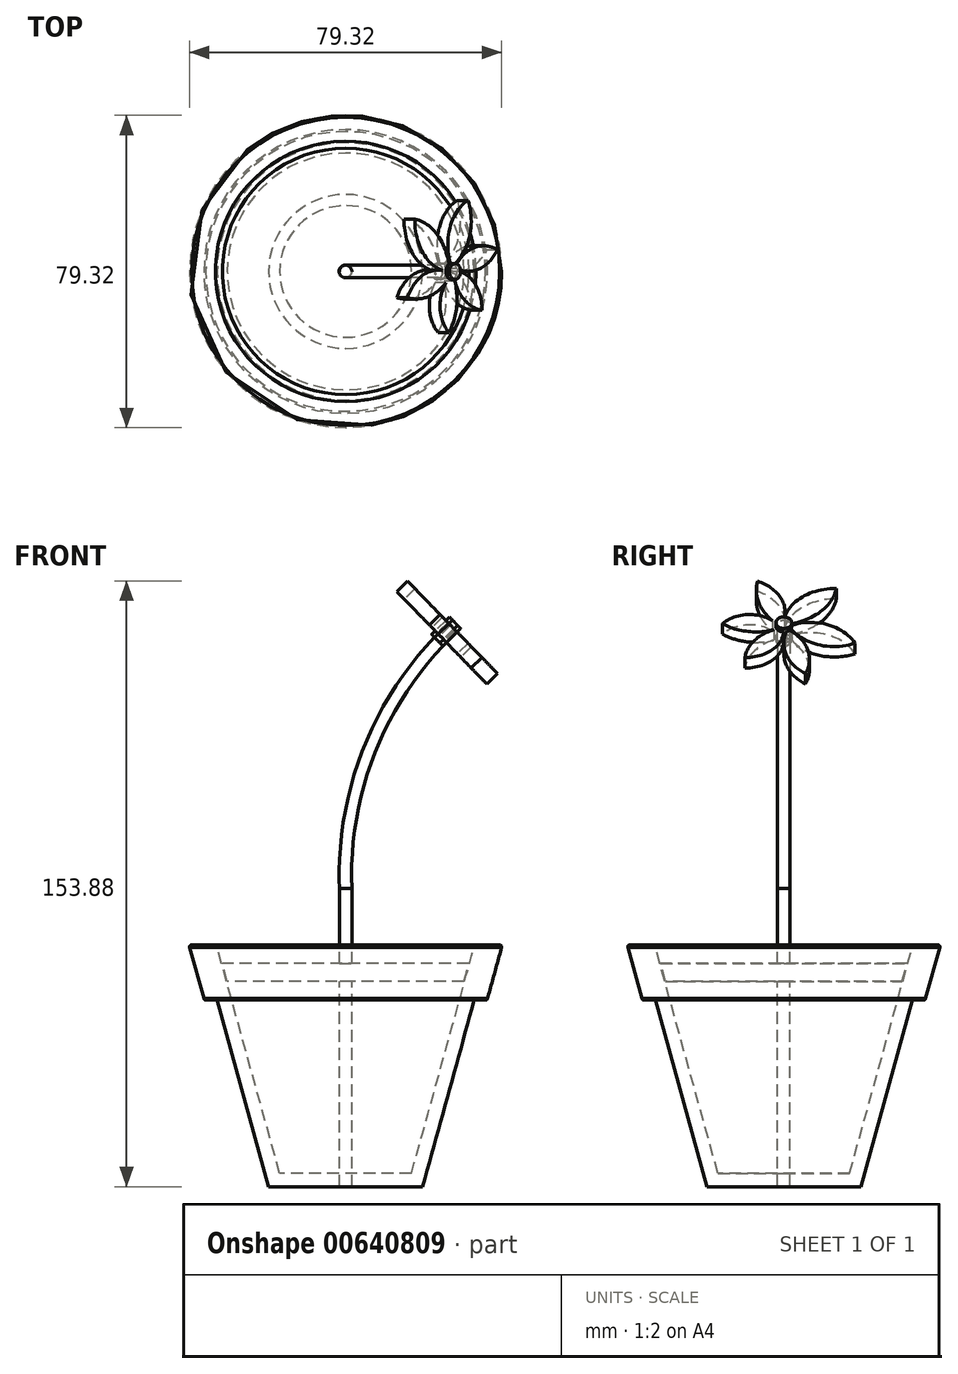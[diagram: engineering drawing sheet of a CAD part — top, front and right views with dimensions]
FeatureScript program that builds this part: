
annotation { "Feature Type Name" : "Feature", "Feature Type Description" : "" }
export const myFeature = defineFeature(function(context is Context, id is Id, definition is map)
    precondition{}
    {
        {
            var Q0;
            Q0=qCreatedBy(makeId("Front.planeOp"),FACE);
            var sketch = newSketch(context, id + "F0", { "sketchPlane" : qUnion([Q0])});
            skLineSegment(sketch, "E0", {"start": v(0, 0) * mm, "end": v(-19.55, 0) * mm});
            skLineSegment(sketch, "E1", {"start": v(0, 0) * mm, "end": v(0, 63.38) * mm});
            skLineSegment(sketch, "E2", {"start": v(-32.67, 47.4) * mm, "end": v(-19.55, 0) * mm});
            skLineSegment(sketch, "E3", {"start": v(-39.64, 60.78) * mm, "end": v(-36.03, 47.77) * mm});
            skLineSegment(sketch, "E4", {"start": v(-35.54, 47.4) * mm, "end": v(-32.67, 47.4) * mm});
            skLineSegment(sketch, "E5", {"start": v(-39.15, 61.42) * mm, "end": v(-33.1, 61.42) * mm});
            skLineSegment(sketch, "E6", {"start": v(-32.73, 61.15) * mm, "end": v(-16.73, 3.38) * mm});
            skLineSegment(sketch, "E7", {"start": v(-16.73, 3.38) * mm, "end": v(0, 3.38) * mm});
            skLineSegment(sketch, "E8", {"start": v(0, 3.38) * mm, "end": v(0, 0) * mm});
            skPoint(sketch, "E9.visualSharp", {"position": v(-39.81, 61.42) * mm});
            skArc(sketch, "E9.filletArc", {"start": v(-39.15, 61.42) * mm, "mid": v(-39.55, 61.22) * mm, "end": v(-39.64, 60.78) * mm});
            skPoint(sketch, "E10.visualSharp", {"position": v(-35.93, 47.4) * mm});
            skArc(sketch, "E10.filletArc", {"start": v(-36.03, 47.77) * mm, "mid": v(-35.85, 47.5) * mm, "end": v(-35.54, 47.4) * mm});
            skPoint(sketch, "E11.visualSharp", {"position": v(-32.81, 61.42) * mm});
            skArc(sketch, "E11.filletArc", {"start": v(-32.73, 61.15) * mm, "mid": v(-32.87, 61.35) * mm, "end": v(-33.1, 61.42) * mm});
            skSolve(sketch);
        }
        {
            var Q0;
            Q0=makeQuery(id+"F0.imprint","IMPRINT",FACE,{"disambiguationData":[TD([[makeQuery(id+"F0.imprint","IMPRINT",EDGE,{"derivedFrom":sQuery(id+"F0.wireOp",EDGE,"E0")}),-1.0]])]});
            var Q1;
            Q1=sQuery(id+"F0.wireOp",EDGE,"E8");
            revolve(context, id + "F1", {"entities" : qUnion([Q0]), "axis" : qUnion([Q1]), "revolveType" : RevolveType.FULL});
        }
        {
            var Q0;
            Q0=qCreatedBy(makeId("Front.planeOp"),FACE);
            var sketch = newSketch(context, id + "F2", { "sketchPlane" : qUnion([Q0])});
            skLineSegment(sketch, "E12", {"start": v(0, 3.35) * mm, "end": v(0, 79.16) * mm});
            skArc(sketch, "E13", {"start": v(26.04, 140.8) * mm, "mid": v(6.78, 112.61) * mm, "end": v(0, 79.16) * mm});
            skSolve(sketch);
        }
        {
            var Q0;
            Q0=qCreatedBy(makeId("Top.planeOp"),FACE);
            var sketch = newSketch(context, id + "F3", { "sketchPlane" : qUnion([Q0])});
            skCircle(sketch, "E14", {"center": v(0, 0) * mm, "radius": 1.58 * mm});
            skSolve(sketch);
        }
        {
            var Q0;
            Q0=makeQuery(id+"F3.imprint","IMPRINT",FACE,{"disambiguationData":[TD([[makeQuery(id+"F3.imprint","IMPRINT",EDGE,{"derivedFrom":sQuery(id+"F3.wireOp",EDGE,"E14")}),1.0]])]});
            var Q1;
            Q1=sQuery(id+"F2.wireOp",EDGE,"E12");
            var Q2;
            Q2=sQuery(id+"F2.wireOp",EDGE,"E13");
            sweep(context, id + "F4", {"profiles" : qUnion([Q0]), "path" : qUnion([Q1, Q2])});
        }
        {
            var Q0;
            Q0=makeQuery(id+"F4.opSweep","CAP_FACE",FACE,{"disambiguationData":[OSD([sQuery(id+"F2.wireOp",VERTEX,"E13.start"),sQuery(id+"F3.wireOp",EDGE,"E14")])],"isStart":false});
            cPlane(context, id + "F5", {"entities" : qUnion([Q0]), "cplaneType" : CPlaneType.OFFSET, "offset" : 1.27 * mm, "width" : 152.4 * mm, "height" : 152.4 * mm});
        }
        {
            var Q0;
            Q0=qCreatedBy(id+"F5.planeOp",FACE);
            var sketch = newSketch(context, id + "F6", { "sketchPlane" : qUnion([Q0])});
            skCircle(sketch, "E15", {"center": v(0, 83.3) * mm, "radius": 2.03 * mm});
            skArc(sketch, "E16", {"start": v(13.33, 96.65) * mm, "mid": v(4.5, 93.53) * mm, "end": v(0, 85.33) * mm});
            skArc(sketch, "E17", {"start": v(1.81, 84.2) * mm, "mid": v(9.5, 88.64) * mm, "end": v(13.33, 96.65) * mm});
            skArc(sketch, "E18", {"start": v(18.04, 77.24) * mm, "mid": v(11.26, 83.82) * mm, "end": v(1.81, 83.56) * mm});
            skArc(sketch, "E19", {"start": v(1.81, 82.4) * mm, "mid": v(8.93, 76.69) * mm, "end": v(18.04, 77.24) * mm});
            skArc(sketch, "E20", {"start": v(5.47, 66.5) * mm, "mid": v(6.1, 74.88) * mm, "end": v(1.43, 81.86) * mm});
            skArc(sketch, "E21", {"start": v(0.65, 81.38) * mm, "mid": v(0.66, 73.16) * mm, "end": v(5.47, 66.5) * mm});
            skArc(sketch, "E22", {"start": v(-9.88, 72.2) * mm, "mid": v(-3.14, 74.77) * mm, "end": v(0, 81.27) * mm});
            skArc(sketch, "E23", {"start": v(-1.8, 82.37) * mm, "mid": v(-7.3, 78.45) * mm, "end": v(-9.88, 72.2) * mm});
            skArc(sketch, "E24", {"start": v(-15.56, 84.23) * mm, "mid": v(-8.94, 81.42) * mm, "end": v(-1.8, 82.37) * mm});
            skArc(sketch, "E25", {"start": v(-1.8, 84.23) * mm, "mid": v(-8.68, 87.47) * mm, "end": v(-15.56, 84.23) * mm});
            skArc(sketch, "E26", {"start": v(-6.68, 99.33) * mm, "mid": v(-6.21, 91.14) * mm, "end": v(-1.8, 84.23) * mm});
            skArc(sketch, "E27", {"start": v(0, 85.33) * mm, "mid": v(-0.86, 93.51) * mm, "end": v(-6.68, 99.33) * mm});
            skSolve(sketch);
        }
        {
            var Q0;
            {var subQ0=sQuery(id+"F6.wireOp",EDGE,"E15");var subQ11=makeQuery(id+"F6.imprint","INTERSECT",VERTEX,{"derivedFrom":[subQ0,sQuery(id+"F6.wireOp",EDGE,"E17")]});Q0=makeQuery(id+"F6.imprint","IMPRINT",FACE,{"disambiguationData":[TD([[makeQuery(id+"F6.imprint","IMPRINT",EDGE,{"disambiguationData":[TD([[subQ11,1.0]])],"derivedFrom":subQ0}),1.0]])]});}
            extrude(context, id + "F7", {"entities" : qUnion([Q0]), "endBound" : BoundingType.SYMMETRIC, "depth" : 2.54 * mm, "offsetDistance" : 25.4 * mm});
        }
        {
            var Q0;
            Q0 = qSketchRegion(id + "F6", true);
            var Q1;
            Q1=makeQuery(id+"F7.opExtrude","CAP_FACE",FACE,{"disambiguationData":[OSD([sQuery(id+"F6.wireOp",EDGE,"E15"),sQuery(id+"F6.wireOp",EDGE,"E25"),sQuery(id+"F6.wireOp",EDGE,"E26")])],"isStart":false});
            extrude(context, id + "F8", {"entities" : qUnion([Q0, Q1]), "operationType" : NewBodyOperationType.ADD, "depth" : 3.8 * mm, "offsetDistance" : 25.4 * mm});
        }
        {
            var Q0;
            Q0=qCreatedBy(makeId("Front.planeOp"),FACE);
            var sketch = newSketch(context, id + "F9", { "sketchPlane" : qUnion([Q0])});
            skLineSegment(sketch, "E28", {"start": v(0, 52.13) * mm, "end": v(-30.06, 52.13) * mm});
            skLineSegment(sketch, "E29", {"start": v(-30.06, 52.13) * mm, "end": v(-31.31, 56.66) * mm});
            skLineSegment(sketch, "E30", {"start": v(-31.31, 56.66) * mm, "end": v(0, 56.66) * mm});
            skLineSegment(sketch, "E31", {"start": v(0, 56.66) * mm, "end": v(0, 52.13) * mm});
            skSolve(sketch);
        }
        {
            var Q0;
            Q0=makeQuery(id+"F9.imprint","IMPRINT",FACE,{"disambiguationData":[TD([[makeQuery(id+"F9.imprint","IMPRINT",EDGE,{"derivedFrom":sQuery(id+"F9.wireOp",EDGE,"E28")}),-1.0]])]});
            var Q1;
            Q1=sQuery(id+"F9.wireOp",EDGE,"E31");
            revolve(context, id + "F10", {"operationType" : NewBodyOperationType.ADD, "entities" : qUnion([Q0]), "axis" : qUnion([Q1]), "revolveType" : RevolveType.FULL});
        }
    });
